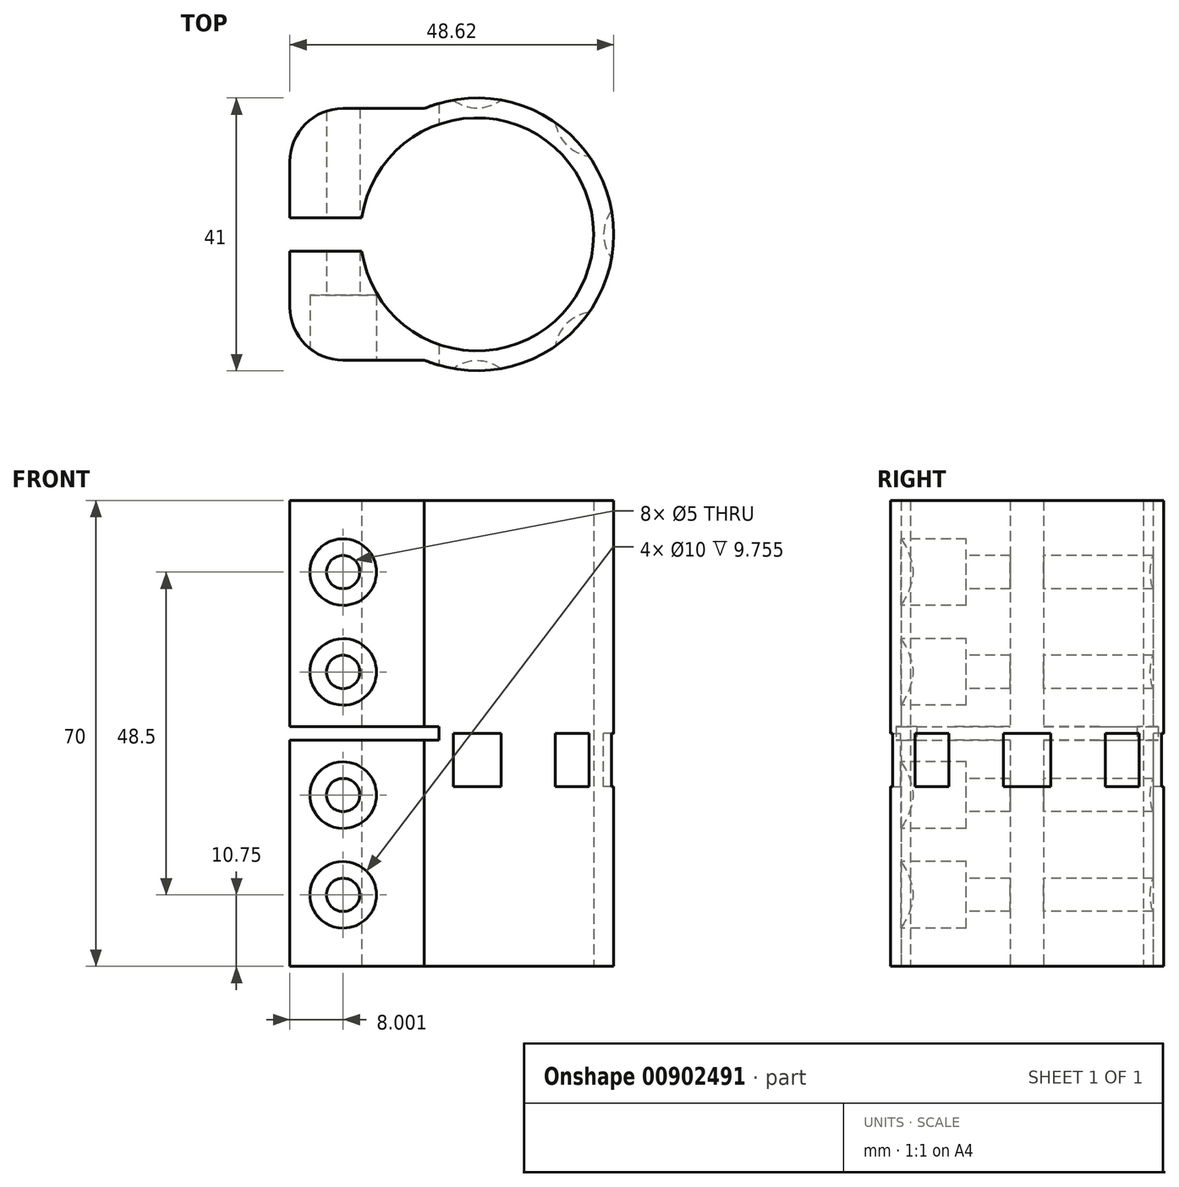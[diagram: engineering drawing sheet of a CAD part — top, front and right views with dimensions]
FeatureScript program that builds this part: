
annotation { "Feature Type Name" : "Feature", "Feature Type Description" : "" }
export const myFeature = defineFeature(function(context is Context, id is Id, definition is map)
    precondition{}
    {
        {
            var Q0;
            Q0=qCreatedBy(makeId("Top.planeOp"),FACE);
            var sketch = newSketch(context, id + "F0", { "sketchPlane" : qUnion([Q0])});
            skArc(sketch, "E0", {"start": v(-17.32, -2.5) * mm, "mid": v(17.5, 0) * mm, "end": v(-17.32, 2.5) * mm});
            skLineSegment(sketch, "E1", {"start": v(-17.32, 2.5) * mm, "end": v(-28.12, 2.5) * mm});
            skLineSegment(sketch, "E2", {"start": v(-28.12, 2.5) * mm, "end": v(-28.12, 10.9) * mm});
            skLineSegment(sketch, "E3", {"start": v(-20.12, 18.9) * mm, "end": v(-7.92, 18.9) * mm});
            skPoint(sketch, "E4.visualSharp", {"position": v(-28.12, 18.9) * mm});
            skArc(sketch, "E4.filletArc", {"start": v(-20.12, 18.9) * mm, "mid": v(-25.78, 16.57) * mm, "end": v(-28.12, 10.9) * mm});
            skLineSegment(sketch, "E5.MirrorCS", {"start": v(-20.12, -18.9) * mm, "end": v(-7.92, -18.9) * mm});
            skArc(sketch, "E6.MirrorCS", {"start": v(-20.12, -18.9) * mm, "mid": v(-25.78, -16.57) * mm, "end": v(-28.12, -10.9) * mm});
            skLineSegment(sketch, "E7.MirrorCS", {"start": v(-17.32, -2.5) * mm, "end": v(-28.12, -2.5) * mm});
            skLineSegment(sketch, "E8.MirrorCS", {"start": v(-28.12, -2.5) * mm, "end": v(-28.12, -10.9) * mm});
            skArc(sketch, "E9.trimOffspring", {"start": v(-7.92, -18.9) * mm, "mid": v(20.5, 0) * mm, "end": v(-7.92, 18.9) * mm});
            skSolve(sketch);
        }
        {
            var Q0;
            Q0 = qSketchRegion(id + "F0", true);
            extrude(context, id + "F1", {"entities" : qUnion([Q0]), "endBound" : BoundingType.SYMMETRIC, "depth" : 70 * mm, "offsetDistance" : 25 * mm});
        }
        {
            var Q0;
            Q0=makeQuery(id+"F1.opExtrude","SWEPT_FACE",FACE,{"disambiguationData":[OSD([sQuery(id+"F0.wireOp",EDGE,"E5.MirrorCS")])]});
            var sketch = newSketch(context, id + "F2", { "sketchPlane" : qUnion([Q0])});
            skLineSegment(sketch, "E10", {"start": v(0, 0) * mm, "end": v(0, -71.14) * mm, "construction": true});
            skLineSegment(sketch, "E11", {"start": v(0, -71.14) * mm, "end": v(-20.2, -71.14) * mm, "construction": true});
            skLineSegment(sketch, "E12", {"start": v(-20.2, -71.14) * mm, "end": v(-20.2, 72.15) * mm, "construction": true});
            skPoint(sketch, "E13", {"position": v(-20.12, -24.25) * mm});
            skPoint(sketch, "E14", {"position": v(-20.12, -9.25) * mm});
            skPoint(sketch, "E15", {"position": v(-20.12, 9.25) * mm});
            skPoint(sketch, "E16", {"position": v(-20.12, 24.25) * mm});
            skSolve(sketch);
        }
        {
            var Q0;
            Q0=sQuery(id+"F2.wireOp",VERTEX,"E13");
            var Q1;
            Q1=sQuery(id+"F2.wireOp",VERTEX,"E14");
            var Q2;
            Q2=sQuery(id+"F2.wireOp",VERTEX,"E15");
            var Q3;
            Q3=sQuery(id+"F2.wireOp",VERTEX,"E16");
            var Q4;
            Q4=makeQuery(id+"F1.opExtrude","SWEPT_BODY",BODY,{"disambiguationData":[OSD([sQuery(id+"F0.wireOp",EDGE,"E0"),sQuery(id+"F0.wireOp",EDGE,"E1"),sQuery(id+"F0.wireOp",EDGE,"E2"),sQuery(id+"F0.wireOp",EDGE,"E3"),sQuery(id+"F0.wireOp",EDGE,"E4.filletArc"),sQuery(id+"F0.wireOp",EDGE,"E5.MirrorCS"),sQuery(id+"F0.wireOp",EDGE,"E6.MirrorCS"),sQuery(id+"F0.wireOp",EDGE,"E7.MirrorCS"),sQuery(id+"F0.wireOp",EDGE,"E8.MirrorCS"),sQuery(id+"F0.wireOp",EDGE,"E9.trimOffspring")])]});
            hole(context, id + "F3", {"style" : HoleStyle.C_BORE, "endStyle" : HoleEndStyle.THROUGH, "holeDiameter" : 5 * mm, "cBoreDiameter" : 10 * mm, "cBoreDepth" : 8 * mm, "majorDiameter" : 5 * mm, "isTappedThrough" : true, "tappedDepth" : 12 * mm, "tapClearance" : 3, "locations" : qUnion([Q0, Q1, Q2, Q3]), "scope" : qUnion([Q4])});
        }
        {
            var Q0;
            Q0=qCreatedBy(makeId("Front.planeOp"),FACE);
            var sketch = newSketch(context, id + "F4", { "sketchPlane" : qUnion([Q0])});
            skLineSegment(sketch, "E17.bottom", {"start": v(-28.12, 1) * mm, "end": v(-5.72, 1) * mm});
            skLineSegment(sketch, "E17.top", {"start": v(-28.12, -1) * mm, "end": v(-5.72, -1) * mm});
            skLineSegment(sketch, "E17.left", {"start": v(-28.12, 1) * mm, "end": v(-28.12, -1) * mm});
            skLineSegment(sketch, "E17.right", {"start": v(-5.72, 1) * mm, "end": v(-5.72, -1) * mm});
            skSolve(sketch);
        }
        {
            var Q0;
            Q0 = qSketchRegion(id + "F4", true);
            extrude(context, id + "F5", {"entities" : qUnion([Q0]), "operationType" : NewBodyOperationType.REMOVE, "endBound" : BoundingType.SYMMETRIC, "oppositeDirection" : true, "depth" : 50 * mm, "offsetDistance" : 25 * mm});
        }
        {
            var Q0;
            Q0=qCreatedBy(makeId("Top.planeOp"),FACE);
            var sketch = newSketch(context, id + "F6", { "sketchPlane" : qUnion([Q0])});
            skCircle(sketch, "E18", {"center": v(0, -25) * mm, "radius": 6 * mm});
            skCircle(sketch, "E19.1.0", {"center": v(17.68, -17.68) * mm, "radius": 6 * mm});
            skCircle(sketch, "E19.2.0", {"center": v(25, 0) * mm, "radius": 6 * mm});
            skCircle(sketch, "E19.3.0", {"center": v(17.68, 17.68) * mm, "radius": 6 * mm});
            skCircle(sketch, "E19.4.0", {"center": v(0, 25) * mm, "radius": 6 * mm});
            skPoint(sketch, "E19.center", {"position": v(0, 0) * mm});
            skLineSegment(sketch, "E19.anchor1", {"start": v(0, 0) * mm, "end": v(0, -25) * mm, "construction": true});
            skLineSegment(sketch, "E19.anchor2", {"start": v(0, 0) * mm, "end": v(0, 25) * mm, "construction": true});
            skSolve(sketch);
        }
        {
            var Q0;
            Q0 = qSketchRegion(id + "F6", true);
            extrude(context, id + "F7", {"entities" : qUnion([Q0]), "operationType" : NewBodyOperationType.REMOVE, "oppositeDirection" : true, "depth" : 8 * mm, "offsetDistance" : 25 * mm});
        }
    });
